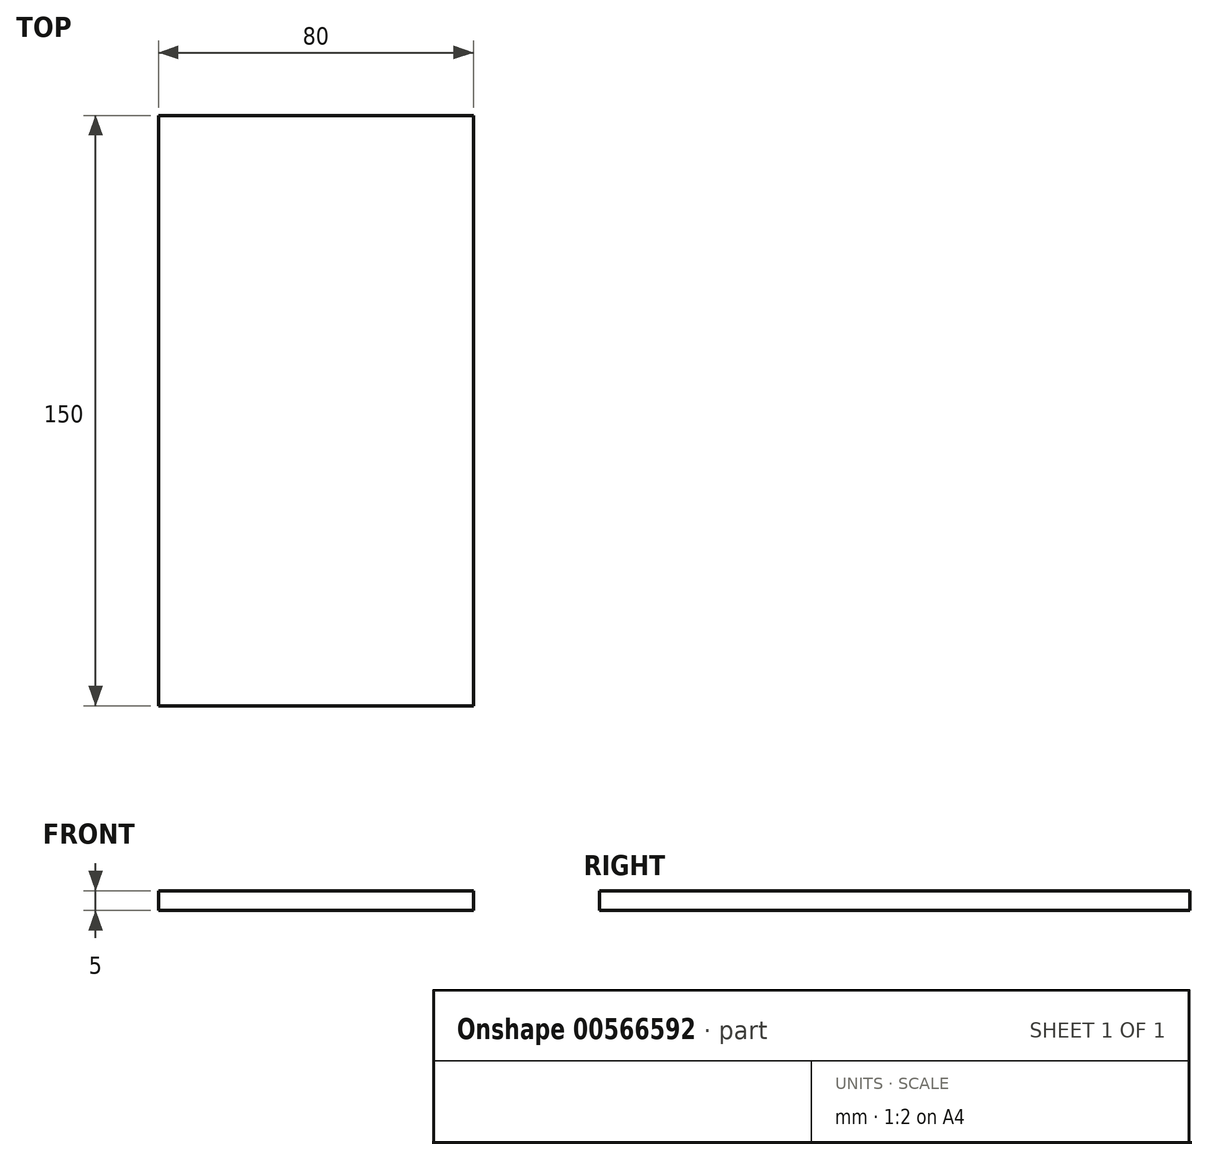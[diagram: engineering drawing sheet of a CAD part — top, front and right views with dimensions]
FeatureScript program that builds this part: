
annotation { "Feature Type Name" : "Feature", "Feature Type Description" : "" }
export const myFeature = defineFeature(function(context is Context, id is Id, definition is map)
    precondition{}
    {
        {
            var Q0;
            Q0=qCreatedBy(makeId("Top.planeOp"),FACE);
            var sketch = newSketch(context, id + "F0", { "sketchPlane" : qUnion([Q0])});
            skLineSegment(sketch, "E0.bottom", {"start": v(0, 0) * mm, "end": v(80, 0) * mm});
            skLineSegment(sketch, "E0.top", {"start": v(0, 150) * mm, "end": v(80, 150) * mm});
            skLineSegment(sketch, "E0.left", {"start": v(0, 0) * mm, "end": v(0, 150) * mm});
            skLineSegment(sketch, "E0.right", {"start": v(80, 0) * mm, "end": v(80, 150) * mm});
            skSolve(sketch);
        }
        {
            var Q0;
            Q0=makeQuery(id+"F0.imprint","IMPRINT",FACE,{"disambiguationData":[TD([[makeQuery(id+"F0.imprint","IMPRINT",EDGE,{"derivedFrom":sQuery(id+"F0.wireOp",EDGE,"E0.bottom")}),1.0]])]});
            extrude(context, id + "F1", {"entities" : qUnion([Q0]), "depth" : 5 * mm, "offsetDistance" : 25 * mm});
        }
    });
